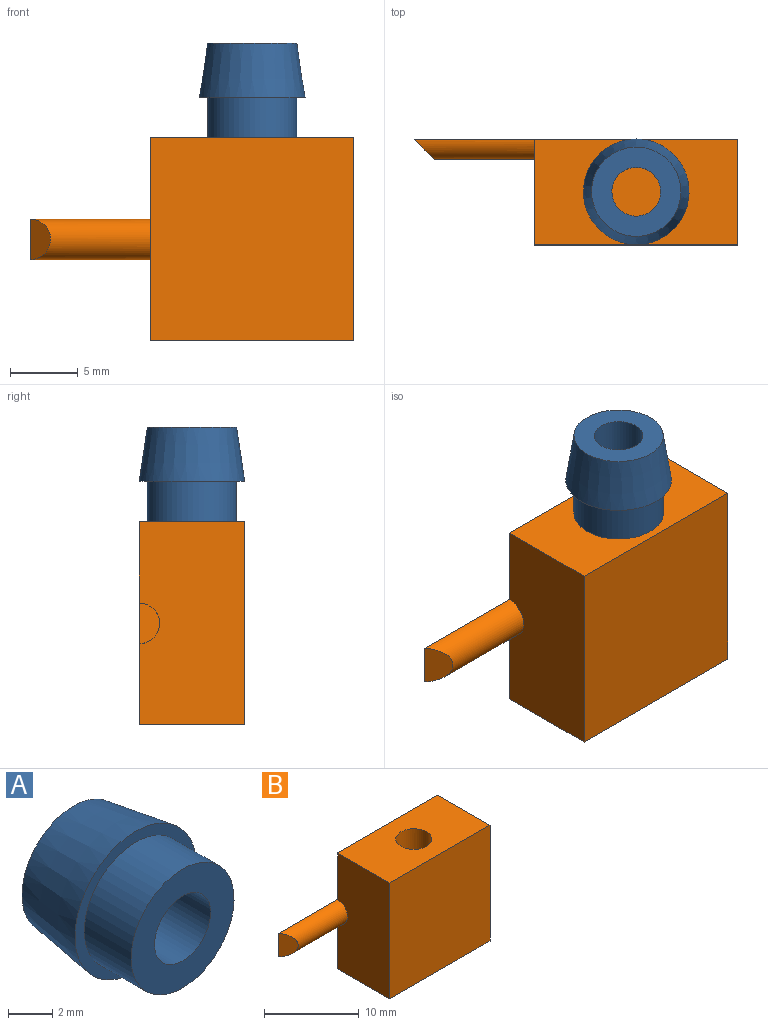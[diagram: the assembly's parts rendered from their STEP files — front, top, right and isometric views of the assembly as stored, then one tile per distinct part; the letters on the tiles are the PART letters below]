
ASSEMBLY  parts=2 mates=1
PART A: 6 faces, bbox 7.8x7x7.8 mm
  f0: plane 6.6x6.6mm, normal (0,-1,0), area 24mm2, adj f4,f5
  f1: plane 6.6x6.6mm, normal (0,1,0), area 24mm2, adj f2,f5
  f2: cone r=3.9mm half-angle=8.5deg, axis (0,-1,0), area 91.5mm2, adj f1,f3
  f3: plane 7.8x7.8mm, normal (0,-1,0), area 13.6mm2, adj f2,f4
  f4: cylinder r=3.3mm len=6.6mm, axis (0,1,0), area 62.2mm2, adj f0,f3
  f5: cylinder r=1.8mm len=7mm, axis (0,1,0), area 79.2mm2, adj f0,f1
PART B: 11 faces, bbox 23.9x7.8x15 mm
  f0: plane 15x15mm, normal (0,-1,0), area 225mm2, adj f1,f3,f4,f5
  f1: plane 15x7.8mm, normal (1,0,0), area 117mm2, adj f0,f2,f4,f5
  f2: plane 23.9x15mm, normal (0,1,0), area 246.4mm2, adj f1,f3,f4,f5,f8,f9,f10
  f3: plane 15x7.8mm, normal (-1,0,0), area 113.5mm2, adj f0,f2,f4,f5,f9
  f4: plane 15x7.8mm, normal (0,0,1), area 105.7mm2, adj f0,f1,f2,f3,f6
  f5: plane 15x7.8mm, normal (0,0,-1), area 117mm2, adj f0,f1,f2,f3
  f6: cylinder r=1.9mm len=13mm, axis (0,0,1), area 149.5mm2, adj f4,f7,f8
  f7: plane 3.8x3.8mm, normal (0,0,1), area 11.3mm2, adj f6
  f8: cylinder r=1.3mm len=2.61mm, axis (0,1,0), area 18.4mm2, adj f2,f6
  f9: cylinder r=1.5mm len=8.9mm, axis (1,0,0), area 37.4mm2, adj f2,f3,f10
  f10: plane 3x1.5mm, normal (-0.71,-0.71,0), area 5mm2, adj f2,f9
PLACE A rot(axis=(0,0.71,0.71),180deg) t=(0,0,15)mm
PLACE B at identity
MATE fastened B.f6 <-> A.f2  axis (0,0,1) through (0,0,15)mm
